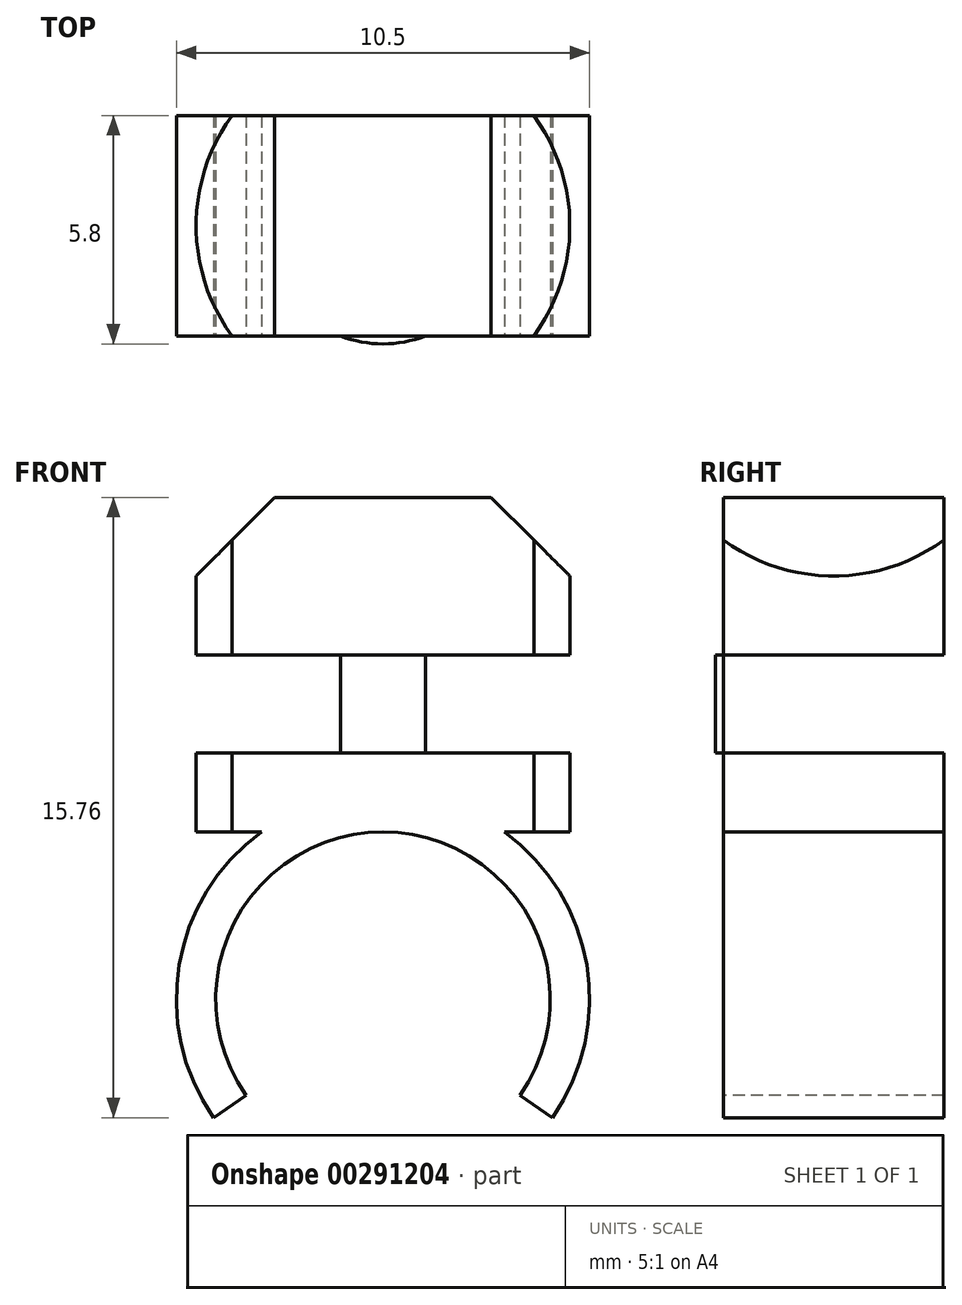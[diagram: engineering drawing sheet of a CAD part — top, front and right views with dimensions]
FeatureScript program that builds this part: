
annotation { "Feature Type Name" : "Feature", "Feature Type Description" : "" }
export const myFeature = defineFeature(function(context is Context, id is Id, definition is map)
    precondition{}
    {
        {
            var Q0;
            Q0=qCreatedBy(makeId("Top.planeOp"),FACE);
            var sketch = newSketch(context, id + "F0", { "sketchPlane" : qUnion([Q0])});
            skArc(sketch, "E0", {"start": v(-3.84, 2.8) * mm, "mid": v(-4.75, 0) * mm, "end": v(-3.84, -2.8) * mm});
            skLineSegment(sketch, "E1", {"start": v(-3.84, 2.8) * mm, "end": v(3.84, 2.8) * mm});
            skLineSegment(sketch, "E2", {"start": v(-3.84, -2.8) * mm, "end": v(3.84, -2.8) * mm});
            skArc(sketch, "E3.trimOffspring", {"start": v(3.84, -2.8) * mm, "mid": v(4.75, 0) * mm, "end": v(3.84, 2.8) * mm});
            skSolve(sketch);
        }
        {
            var Q0;
            Q0=makeQuery(id+"F0.imprint","IMPRINT",FACE,{"disambiguationData":[TD([[makeQuery(id+"F0.imprint","IMPRINT",EDGE,{"derivedFrom":sQuery(id+"F0.wireOp",EDGE,"E0")}),1.0]])]});
            extrude(context, id + "F1", {"entities" : qUnion([Q0]), "depth" : 4 * mm});
        }
        {
            var Q0;
            Q0=makeQuery(id+"F1.opExtrude","CAP_FACE",FACE,{"disambiguationData":[OSD([sQuery(id+"F0.wireOp",EDGE,"E0"),sQuery(id+"F0.wireOp",EDGE,"E1"),sQuery(id+"F0.wireOp",EDGE,"E2"),sQuery(id+"F0.wireOp",EDGE,"E3.trimOffspring")])],"isStart":true});
            var sketch = newSketch(context, id + "F2", { "sketchPlane" : qUnion([Q0])});
            skCircle(sketch, "E4", {"center": v(0, 0) * mm, "radius": 3 * mm});
            skSolve(sketch);
        }
        {
            var Q0;
            {var subQ0=sQuery(id+"F2.wireOp",EDGE,"E4");var subQ1=makeQuery(id+"F1.opExtrude","CAP_EDGE",EDGE,{"disambiguationData":[OSD([sQuery(id+"F0.wireOp",EDGE,"E2")])],"isStart":true});var subQ2=makeQuery(id+"F2.imprint","INTERSECT",VERTEX,{"disambiguationData":[OD(0.0)],"derivedFrom":[subQ1,subQ0]});Q0=makeQuery(id+"F2.imprint","IMPRINT",FACE,{"disambiguationData":[TD([[makeQuery(id+"F2.imprint","IMPRINT",EDGE,{"disambiguationData":[TD([[subQ2,-1.0]])],"derivedFrom":subQ0}),1.0]])]});}
            extrude(context, id + "F3", {"entities" : qUnion([Q0]), "operationType" : NewBodyOperationType.ADD, "depth" : 2.5 * mm});
        }
        {
            var Q0;
            Q0=makeQuery(id+"F3.opExtrude","CAP_FACE",FACE,{"disambiguationData":[OSD([sQuery(id+"F0.wireOp",EDGE,"E1"),sQuery(id+"F0.wireOp",EDGE,"E2"),sQuery(id+"F2.wireOp",EDGE,"E4")])],"isStart":false});
            var sketch = newSketch(context, id + "F4", { "sketchPlane" : qUnion([Q0])});
            skArc(sketch, "E5.0", {"start": v(3.84, 2.8) * mm, "mid": v(4.75, 0) * mm, "end": v(3.84, -2.8) * mm});
            skLineSegment(sketch, "E6.0", {"start": v(1.08, -2.8) * mm, "end": v(3.84, -2.8) * mm});
            skLineSegment(sketch, "E7.0", {"start": v(-1.08, -2.8) * mm, "end": v(1.08, -2.8) * mm});
            skLineSegment(sketch, "E8.0", {"start": v(-3.84, -2.8) * mm, "end": v(-1.08, -2.8) * mm});
            skArc(sketch, "E9.0", {"start": v(-3.84, -2.8) * mm, "mid": v(-4.75, 0) * mm, "end": v(-3.84, 2.8) * mm});
            skLineSegment(sketch, "E10.0", {"start": v(-3.84, 2.8) * mm, "end": v(-1.08, 2.8) * mm});
            skLineSegment(sketch, "E11.0", {"start": v(-1.08, 2.8) * mm, "end": v(1.08, 2.8) * mm});
            skLineSegment(sketch, "E12.0", {"start": v(1.08, 2.8) * mm, "end": v(3.84, 2.8) * mm});
            skSolve(sketch);
        }
        {
            var Q0;
            Q0 = qSketchRegion(id + "F4", true);
            extrude(context, id + "F5", {"entities" : qUnion([Q0]), "operationType" : NewBodyOperationType.ADD, "depth" : 2 * mm});
        }
        {
            var Q0;
            {var subQ0=sQuery(id+"F0.wireOp",EDGE,"E2");Q0=makeQuery(id+"F5.boolean.opBoolean","MERGE",FACE,{"derivedFrom":[makeQuery(id+"F3.boolean.opBoolean","MERGE",FACE,{"derivedFrom":[makeQuery(id+"F1.opExtrude","SWEPT_FACE",FACE,{"disambiguationData":[OSD([subQ0])]}),makeQuery(id+"F3.opExtrude","SWEPT_FACE",FACE,{"disambiguationData":[OSD([subQ0])]})]}),makeQuery(id+"F5.opExtrude","SWEPT_FACE",FACE,{"disambiguationData":[OSD([sQuery(id+"F4.wireOp",EDGE,"E10.0"),sQuery(id+"F4.wireOp",EDGE,"E11.0"),sQuery(id+"F4.wireOp",EDGE,"E12.0")])]})]});}
            var sketch = newSketch(context, id + "F6", { "sketchPlane" : qUnion([Q0])});
            skCircle(sketch, "E13", {"center": v(0, -8.75) * mm, "radius": 4.25 * mm});
            skCircle(sketch, "E14", {"center": v(0, -8.75) * mm, "radius": 5.25 * mm});
            skLineSegment(sketch, "E15", {"start": v(0, -8.75) * mm, "end": v(-11.33, -16.68) * mm});
            skLineSegment(sketch, "E16", {"start": v(0, -8.75) * mm, "end": v(8.98, -15.04) * mm});
            skSolve(sketch);
        }
        {
            var Q0;
            {var subQ0=sQuery(id+"F6.wireOp",EDGE,"E16");var subQ5=sQuery(id+"F6.wireOp",EDGE,"E14");var subQ6=makeQuery(id+"F6.imprint","INTERSECT",VERTEX,{"derivedFrom":[subQ5,subQ0]});Q0=makeQuery(id+"F6.imprint","IMPRINT",FACE,{"disambiguationData":[TD([[makeQuery(id+"F6.imprint","IMPRINT",EDGE,{"disambiguationData":[TD([[subQ6,1.0]])],"derivedFrom":subQ0}),1.0]])]});}
            var Q1;
            {var subQ0=sQuery(id+"F6.wireOp",EDGE,"E15");var subQ5=sQuery(id+"F6.wireOp",EDGE,"E14");var subQ6=makeQuery(id+"F6.imprint","INTERSECT",VERTEX,{"derivedFrom":[subQ5,subQ0]});Q1=makeQuery(id+"F6.imprint","IMPRINT",FACE,{"disambiguationData":[TD([[makeQuery(id+"F6.imprint","IMPRINT",EDGE,{"disambiguationData":[TD([[subQ6,1.0]])],"derivedFrom":subQ0}),-1.0]])]});}
            extrude(context, id + "F7", {"entities" : qUnion([Q0, Q1]), "operationType" : NewBodyOperationType.ADD, "oppositeDirection" : true, "depth" : 5.6 * mm});
        }
        {
            var Q0;
            {var subQ0=sQuery(id+"F6.wireOp",EDGE,"E14");var subQ1=sQuery(id+"F6.wireOp",EDGE,"E13");var subQ2=sQuery(id+"F4.wireOp",EDGE,"E12.0");var subQ3=sQuery(id+"F4.wireOp",EDGE,"E11.0");var subQ4=sQuery(id+"F4.wireOp",EDGE,"E10.0");var subQ5=sQuery(id+"F0.wireOp",EDGE,"E1");Q0=makeQuery(id+"F7.boolean.opBoolean","MERGE",FACE,{"derivedFrom":[makeQuery(id+"F5.boolean.opBoolean","MERGE",FACE,{"derivedFrom":[makeQuery(id+"F3.boolean.opBoolean","MERGE",FACE,{"derivedFrom":[makeQuery(id+"F1.opExtrude","SWEPT_FACE",FACE,{"disambiguationData":[OSD([subQ5])]}),makeQuery(id+"F3.opExtrude","SWEPT_FACE",FACE,{"disambiguationData":[OSD([subQ5])]})]}),makeQuery(id+"F5.opExtrude","SWEPT_FACE",FACE,{"disambiguationData":[OSD([sQuery(id+"F4.wireOp",EDGE,"E6.0"),sQuery(id+"F4.wireOp",EDGE,"E7.0"),sQuery(id+"F4.wireOp",EDGE,"E8.0")])]})]}),makeQuery(id+"F7.opExtrude","CAP_FACE",FACE,{"disambiguationData":[OSD([subQ4,subQ3,subQ2,subQ1,subQ0,sQuery(id+"F6.wireOp",EDGE,"E15")])],"isStart":false}),makeQuery(id+"F7.opExtrude","CAP_FACE",FACE,{"disambiguationData":[OSD([subQ4,subQ3,subQ2,subQ1,subQ0,sQuery(id+"F6.wireOp",EDGE,"E16")])],"isStart":false})]});}
            var sketch = newSketch(context, id + "F8", { "sketchPlane" : qUnion([Q0])});
            skLineSegment(sketch, "E17", {"start": v(4.75, 4) * mm, "end": v(4.75, 0) * mm});
            skLineSegment(sketch, "E18.0", {"start": v(3.84, 4) * mm, "end": v(4.75, 4) * mm});
            skLineSegment(sketch, "E19.0", {"start": v(3.84, 4) * mm, "end": v(-3.84, 4) * mm});
            skLineSegment(sketch, "E20.0", {"start": v(-3.84, 4) * mm, "end": v(-4.75, 4) * mm});
            skLineSegment(sketch, "E21", {"start": v(-4.75, 0) * mm, "end": v(-4.75, 4) * mm});
            skLineSegment(sketch, "E22", {"start": v(4.75, 2) * mm, "end": v(2.75, 4) * mm});
            skLineSegment(sketch, "E23", {"start": v(-4.75, 2) * mm, "end": v(-2.75, 4) * mm});
            skSolve(sketch);
        }
        {
            var Q0;
            {var subQ0=sQuery(id+"F8.wireOp",EDGE,"E18.0");Q0=makeQuery(id+"F8.imprint","IMPRINT",FACE,{"disambiguationData":[TD([[makeQuery(id+"F8.imprint","IMPRINT",EDGE,{"derivedFrom":subQ0}),-1.0]])]});}
            var Q1;
            {var subQ0=sQuery(id+"F8.wireOp",EDGE,"E19.0");var subQ3=sQuery(id+"F8.wireOp",EDGE,"E22");var subQ4=makeQuery(id+"F8.imprint","INTERSECT",VERTEX,{"derivedFrom":[subQ0,subQ3]});Q1=makeQuery(id+"F8.imprint","IMPRINT",FACE,{"disambiguationData":[TD([[makeQuery(id+"F8.imprint","IMPRINT",EDGE,{"disambiguationData":[TD([[subQ4,1.0]])],"derivedFrom":subQ3}),-1.0]])]});}
            var Q2;
            {var subQ0=sQuery(id+"F8.wireOp",EDGE,"E19.0");var subQ3=sQuery(id+"F8.wireOp",EDGE,"E23");var subQ4=makeQuery(id+"F8.imprint","INTERSECT",VERTEX,{"derivedFrom":[subQ0,subQ3]});Q2=makeQuery(id+"F8.imprint","IMPRINT",FACE,{"disambiguationData":[TD([[makeQuery(id+"F8.imprint","IMPRINT",EDGE,{"disambiguationData":[TD([[subQ4,1.0]])],"derivedFrom":subQ3}),1.0]])]});}
            var Q3;
            {var subQ0=sQuery(id+"F8.wireOp",EDGE,"E20.0");Q3=makeQuery(id+"F8.imprint","IMPRINT",FACE,{"disambiguationData":[TD([[makeQuery(id+"F8.imprint","IMPRINT",EDGE,{"derivedFrom":subQ0}),1.0]])]});}
            extrude(context, id + "F9", {"entities" : qUnion([Q0, Q1, Q2, Q3]), "operationType" : NewBodyOperationType.REMOVE, "oppositeDirection" : true, "depth" : 25 * mm});
        }
    });
